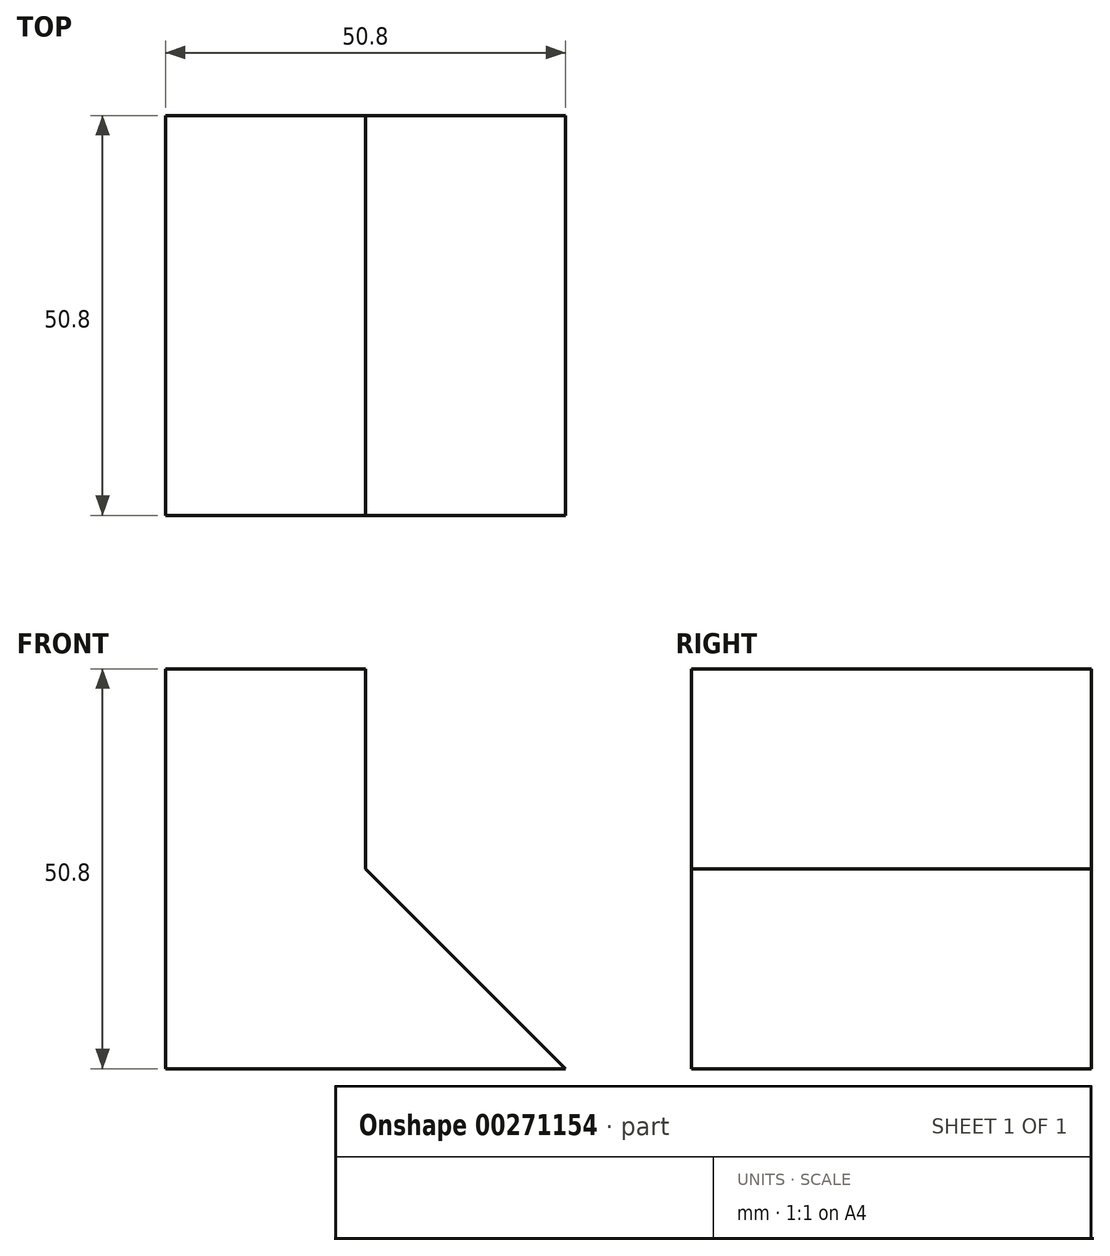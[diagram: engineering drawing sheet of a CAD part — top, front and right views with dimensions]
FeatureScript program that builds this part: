
annotation { "Feature Type Name" : "Feature", "Feature Type Description" : "" }
export const myFeature = defineFeature(function(context is Context, id is Id, definition is map)
    precondition{}
    {
        {
            var Q0;
            Q0=qCreatedBy(makeId("Front.planeOp"),FACE);
            var sketch = newSketch(context, id + "F0", { "sketchPlane" : qUnion([Q0])});
            skLineSegment(sketch, "E0", {"start": v(0, 0) * mm, "end": v(0, 50.8) * mm});
            skLineSegment(sketch, "E1", {"start": v(0, 50.8) * mm, "end": v(-50.8, 50.8) * mm});
            skLineSegment(sketch, "E2", {"start": v(-50.8, 50.8) * mm, "end": v(-50.8, 0) * mm});
            skLineSegment(sketch, "E3", {"start": v(-50.8, 0) * mm, "end": v(0, 0) * mm});
            skLineSegment(sketch, "E4", {"start": v(0, 50.8) * mm, "end": v(-25.4, 50.8) * mm});
            skPoint(sketch, "E5.end.orphan", {"position": v(0, 25.4) * mm});
            skSolve(sketch);
        }
        {
            var Q0;
            Q0 = qSketchRegion(id + "F0", true);
            extrude(context, id + "F1", {"entities" : qUnion([Q0]), "depth" : 50.8 * mm});
        }
        {
            var Q0;
            Q0=qCreatedBy(makeId("Front.planeOp"),FACE);
            var sketch = newSketch(context, id + "F2", { "sketchPlane" : qUnion([Q0])});
            skLineSegment(sketch, "E6", {"start": v(0, 0) * mm, "end": v(0, 25.4) * mm});
            skLineSegment(sketch, "E7", {"start": v(-25.4, 25.4) * mm, "end": v(0, 0) * mm});
            skLineSegment(sketch, "E8", {"start": v(-25.4, 25.4) * mm, "end": v(-25.4, 50.8) * mm});
            skLineSegment(sketch, "E9", {"start": v(-25.4, 50.8) * mm, "end": v(0, 50.8) * mm});
            skLineSegment(sketch, "E10", {"start": v(0, 50.8) * mm, "end": v(0, 25.4) * mm});
            skPoint(sketch, "E11.start.orphan", {"position": v(-25.4, 0) * mm});
            skSolve(sketch);
        }
        {
            var Q0;
            Q0 = qSketchRegion(id + "F2", true);
            extrude(context, id + "F3", {"entities" : qUnion([Q0]), "operationType" : NewBodyOperationType.REMOVE, "depth" : 50.8 * mm});
        }
    });
